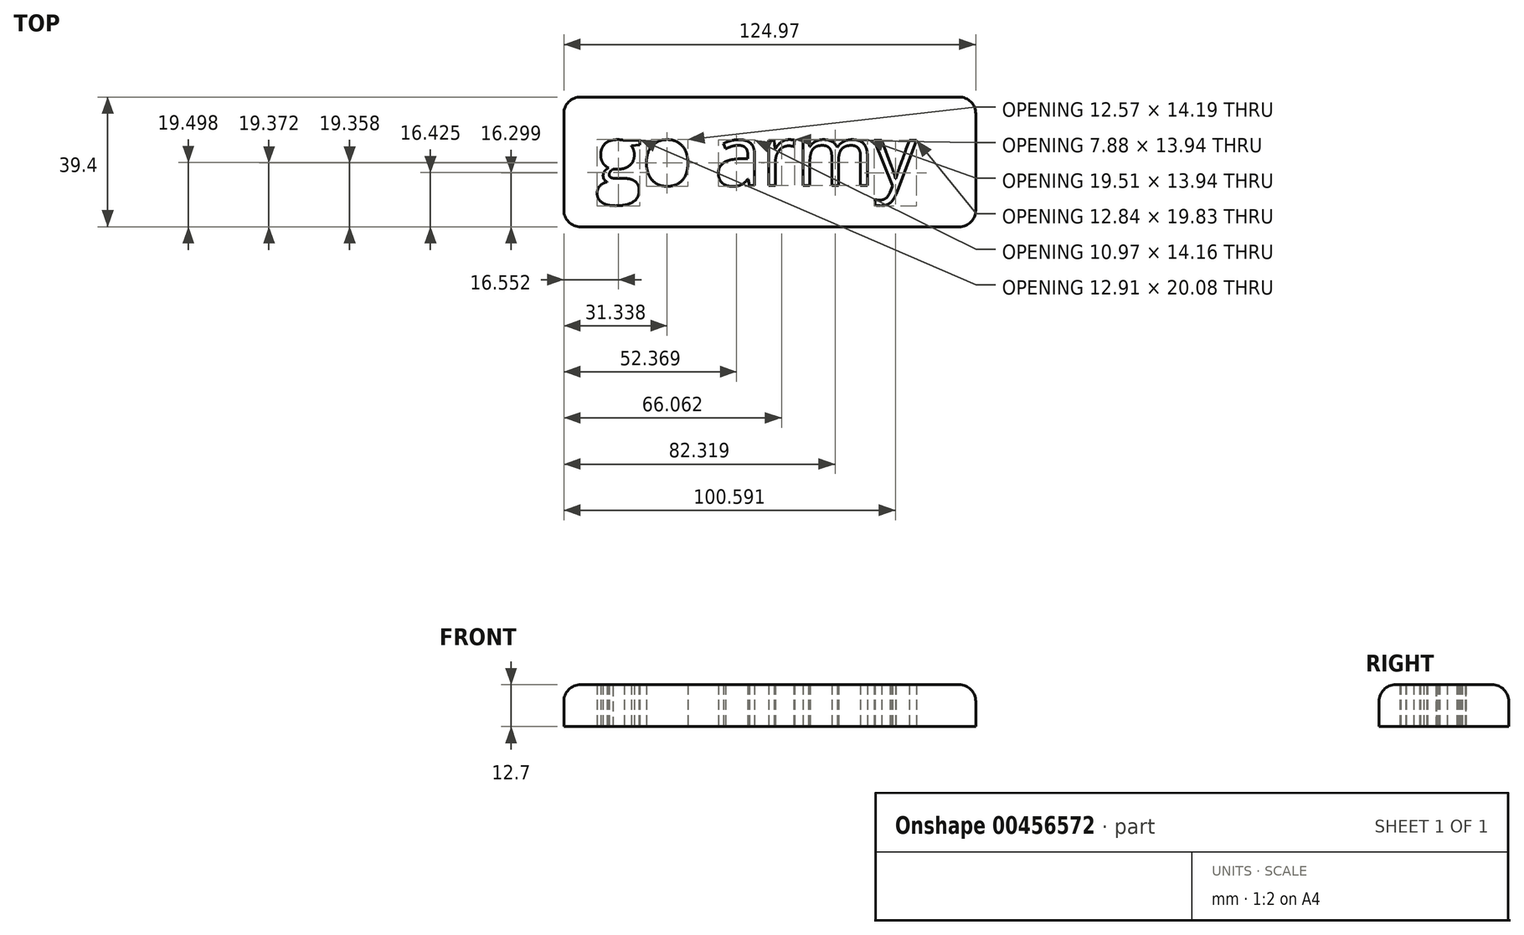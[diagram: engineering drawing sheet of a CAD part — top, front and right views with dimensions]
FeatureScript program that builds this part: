
annotation { "Feature Type Name" : "Feature", "Feature Type Description" : "" }
export const myFeature = defineFeature(function(context is Context, id is Id, definition is map)
    precondition{}
    {
        {
            var Q0;
            Q0=qCreatedBy(makeId("Top.planeOp"),FACE);
            var sketch = newSketch(context, id + "F0", { "sketchPlane" : qUnion([Q0])});
            skText(sketch, "E0", { "text": "go army", "fontName": "OpenSans-Regular.ttf"});
            skPoint(sketch, "E1.end.orphan", {"position": v(50.64, 50.29) * mm});
            skPoint(sketch, "E2.end.orphan", {"position": v(61.66, 50.29) * mm});
            skPoint(sketch, "E3.end.orphan", {"position": v(61.66, 12.16) * mm});
            skPoint(sketch, "E4.start.orphan", {"position": v(-66.02, 0) * mm});
            skLineSegment(sketch, "E5.bottom", {"start": v(-60.3, 39.4) * mm, "end": v(64.66, 39.4) * mm});
            skLineSegment(sketch, "E5.top", {"start": v(-60.3, 0) * mm, "end": v(64.66, 0) * mm});
            skLineSegment(sketch, "E5.left", {"start": v(-60.3, 39.4) * mm, "end": v(-60.3, 0) * mm});
            skLineSegment(sketch, "E5.right", {"start": v(64.66, 39.4) * mm, "end": v(64.66, 0) * mm});
            const initialGuessF0  = {"E0": [-0.0507, 0.01253, 1, 0, 0.01841]};
            skSetInitialGuess(sketch, initialGuessF0);
            skSolve(sketch);
        }
        {
            var Q0;
            Q0=makeQuery(id+"F0.imprint","IMPRINT",FACE,{"disambiguationData":[TD([[makeQuery(id+"F0.imprint","IMPRINT",EDGE,{"derivedFrom":sQuery(id+"F0.wireOp",EDGE,"E0.sketch_text.stroke-0")}),1.0]])]});
            extrude(context, id + "F1", {"entities" : qUnion([Q0]), "depth" : 12.7 * mm});
        }
        {
            var Q0;
            Q0=makeQuery(id+"F1.opExtrude","CAP_EDGE",EDGE,{"disambiguationData":[OSD([sQuery(id+"F0.wireOp",EDGE,"E5.bottom")])],"isStart":false});
            var Q1;
            Q1=makeQuery(id+"F1.opExtrude","CAP_EDGE",EDGE,{"disambiguationData":[OSD([sQuery(id+"F0.wireOp",EDGE,"E5.left")])],"isStart":false});
            var Q2;
            Q2=makeQuery(id+"F1.opExtrude","CAP_EDGE",EDGE,{"disambiguationData":[OSD([sQuery(id+"F0.wireOp",EDGE,"E5.right")])],"isStart":false});
            var Q3;
            Q3=makeQuery(id+"F1.opExtrude","CAP_EDGE",EDGE,{"disambiguationData":[OSD([sQuery(id+"F0.wireOp",EDGE,"E5.top")])],"isStart":false});
            fillet(context, id + "F2", {"entities" : qUnion([Q0, Q1, Q2, Q3]), "radius" : 5.08 * mm, "tangentPropagation" : true, "allowEdgeOverflow" : false});
        }
        {
            var Q0;
            Q0=makeQuery(id+"F1.opExtrude","SWEPT_EDGE",EDGE,{"disambiguationData":[OSD([sQuery(id+"F0.wireOp",EDGE,"E5.top"),sQuery(id+"F0.wireOp",EDGE,"E5.right")])]});
            var Q1;
            Q1=makeQuery(id+"F1.opExtrude","SWEPT_EDGE",EDGE,{"disambiguationData":[OSD([sQuery(id+"F0.wireOp",EDGE,"E5.top"),sQuery(id+"F0.wireOp",EDGE,"E5.left")])]});
            var Q2;
            Q2=makeQuery(id+"F1.opExtrude","SWEPT_EDGE",EDGE,{"disambiguationData":[OSD([sQuery(id+"F0.wireOp",EDGE,"E5.bottom"),sQuery(id+"F0.wireOp",EDGE,"E5.left")])]});
            var Q3;
            Q3=makeQuery(id+"F1.opExtrude","SWEPT_EDGE",EDGE,{"disambiguationData":[OSD([sQuery(id+"F0.wireOp",EDGE,"E5.bottom"),sQuery(id+"F0.wireOp",EDGE,"E5.right")])]});
            fillet(context, id + "F3", {"entities" : qUnion([Q0, Q1, Q2, Q3]), "radius" : 5.08 * mm, "tangentPropagation" : true, "allowEdgeOverflow" : false});
        }
    });
